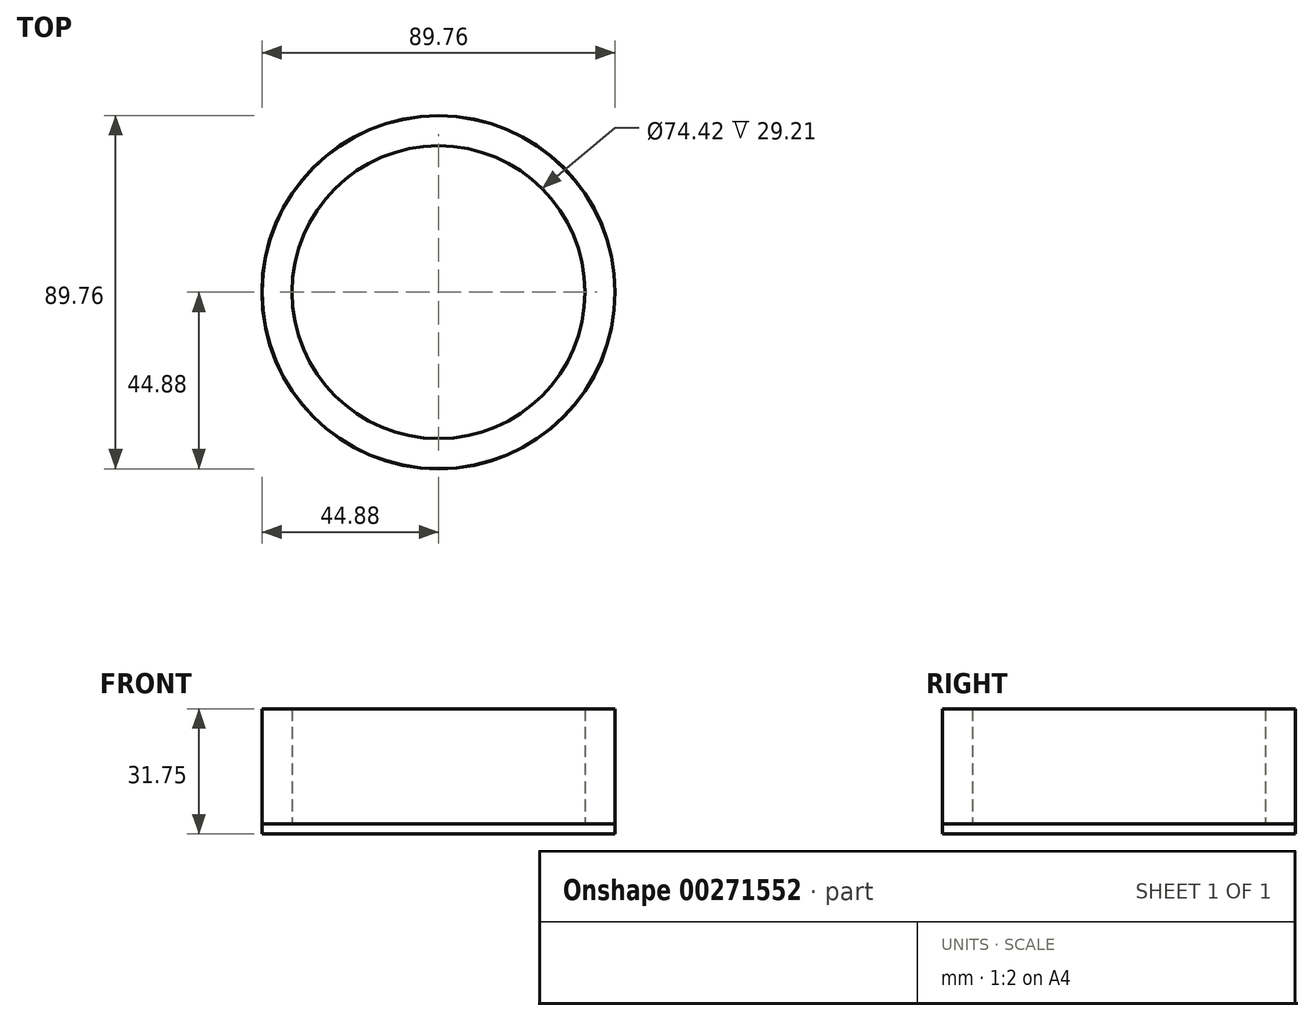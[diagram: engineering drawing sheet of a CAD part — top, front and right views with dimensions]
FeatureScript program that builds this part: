
annotation { "Feature Type Name" : "Feature", "Feature Type Description" : "" }
export const myFeature = defineFeature(function(context is Context, id is Id, definition is map)
    precondition{}
    {
        {
            var Q0;
            Q0=qCreatedBy(makeId("Top.planeOp"),FACE);
            var sketch = newSketch(context, id + "F0", { "sketchPlane" : qUnion([Q0])});
            skCircle(sketch, "E0", {"center": v(0, 0) * mm, "radius": 44.83 * mm});
            skCircle(sketch, "E1", {"center": v(0, 0) * mm, "radius": 37.2 * mm});
            skSolve(sketch);
        }
        {
            var Q0;
            Q0=makeQuery(id+"F0.imprint","IMPRINT",FACE,{"disambiguationData":[TD([[makeQuery(id+"F0.imprint","IMPRINT",EDGE,{"derivedFrom":sQuery(id+"F0.wireOp",EDGE,"E0")}),1.0]])]});
            extrude(context, id + "F1", {"entities" : qUnion([Q0]), "depth" : 31.75 * mm});
        }
        {
            var Q0;
            Q0=qCreatedBy(makeId("Top.planeOp"),FACE);
            var sketch = newSketch(context, id + "F2", { "sketchPlane" : qUnion([Q0])});
            skCircle(sketch, "E2", {"center": v(0, 0) * mm, "radius": 44.88 * mm});
            skSolve(sketch);
        }
        {
            var Q0;
            Q0 = qSketchRegion(id + "F2", true);
            extrude(context, id + "F3", {"entities" : qUnion([Q0]), "operationType" : NewBodyOperationType.ADD, "depth" : 2.54 * mm});
        }
    });
